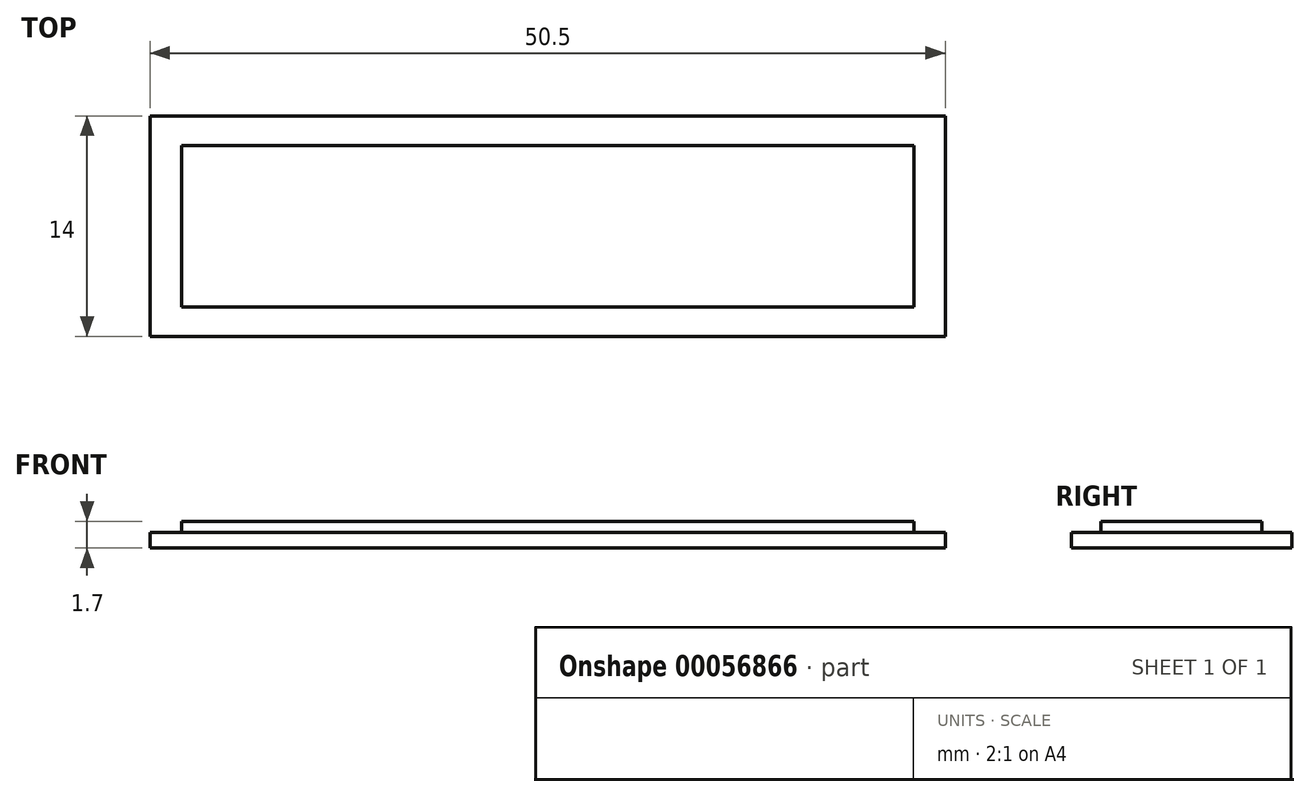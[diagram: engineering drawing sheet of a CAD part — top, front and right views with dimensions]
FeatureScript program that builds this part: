
annotation { "Feature Type Name" : "Feature", "Feature Type Description" : "" }
export const myFeature = defineFeature(function(context is Context, id is Id, definition is map)
    precondition{}
    {
        {
            var Q0;
            Q0=qCreatedBy(makeId("Top.planeOp"),FACE);
            var sketch = newSketch(context, id + "F0", { "sketchPlane" : qUnion([Q0])});
            skLineSegment(sketch, "E0", {"start": v(0, 7) * mm, "end": v(0, -7) * mm, "construction": true});
            skLineSegment(sketch, "E1.0", {"start": v(-23.25, 7) * mm, "end": v(-23.25, -7) * mm, "construction": true});
            skLineSegment(sketch, "E2.0", {"start": v(23.25, 7) * mm, "end": v(23.25, -7) * mm, "construction": true});
            skLineSegment(sketch, "E3", {"start": v(-27.72, 0) * mm, "end": v(23.25, 0) * mm, "construction": true});
            skLineSegment(sketch, "E4.0", {"start": v(-25.25, -7) * mm, "end": v(27.82, -7) * mm, "construction": true});
            skLineSegment(sketch, "E5.0", {"start": v(-25.25, 7) * mm, "end": v(27.82, 7) * mm, "construction": true});
            skLineSegment(sketch, "E6.0", {"start": v(-25.25, -5.12) * mm, "end": v(23.25, -5.12) * mm, "construction": true});
            skLineSegment(sketch, "E7.0", {"start": v(-25.25, 5.12) * mm, "end": v(23.25, 5.12) * mm, "construction": true});
            skLineSegment(sketch, "E8.0", {"start": v(25.25, 7) * mm, "end": v(25.25, -7) * mm, "construction": true});
            skLineSegment(sketch, "E9.0", {"start": v(-25.25, 7) * mm, "end": v(-25.25, -7) * mm, "construction": true});
            skPoint(sketch, "E10.orphan", {"position": v(0, 12.03) * mm});
            skLineSegment(sketch, "E11", {"start": v(-25.25, 7) * mm, "end": v(25.25, 7) * mm});
            skLineSegment(sketch, "E12", {"start": v(25.25, -7) * mm, "end": v(-25.25, -7) * mm});
            skLineSegment(sketch, "E13", {"start": v(-25.25, -7) * mm, "end": v(-25.25, 7) * mm});
            skLineSegment(sketch, "E14", {"start": v(25.25, 7) * mm, "end": v(25.25, -7) * mm});
            skLineSegment(sketch, "E15", {"start": v(23.25, -5.12) * mm, "end": v(23.25, 5.12) * mm});
            skLineSegment(sketch, "E16", {"start": v(23.25, 5.13) * mm, "end": v(-23.25, 5.12) * mm});
            skLineSegment(sketch, "E17", {"start": v(-23.25, 5.12) * mm, "end": v(-23.25, -5.12) * mm});
            skLineSegment(sketch, "E18", {"start": v(-23.25, -5.12) * mm, "end": v(23.25, -5.12) * mm});
            skLineSegment(sketch, "E19.trimOffspring", {"start": v(25.25, -5.12) * mm, "end": v(27.82, -5.12) * mm, "construction": true});
            skLineSegment(sketch, "E20.trimOffspring", {"start": v(25.25, 0) * mm, "end": v(27.82, 0) * mm, "construction": true});
            skLineSegment(sketch, "E21.trimOffspring", {"start": v(25.25, 5.12) * mm, "end": v(27.82, 5.12) * mm, "construction": true});
            skSolve(sketch);
        }
        {
            var Q0;
            Q0=makeQuery(id+"F0.imprint","IMPRINT",FACE,{"disambiguationData":[TD([[makeQuery(id+"F0.imprint","IMPRINT",EDGE,{"derivedFrom":sQuery(id+"F0.wireOp",EDGE,"E15")}),1.0]])]});
            extrude(context, id + "F1", {"entities" : qUnion([Q0]), "depth" : 1.7 * mm});
        }
        {
            var Q0;
            Q0=makeQuery(id+"F0.imprint","IMPRINT",FACE,{"disambiguationData":[TD([[makeQuery(id+"F0.imprint","IMPRINT",EDGE,{"derivedFrom":sQuery(id+"F0.wireOp",EDGE,"E11")}),-1.0]])]});
            extrude(context, id + "F2", {"entities" : qUnion([Q0]), "operationType" : NewBodyOperationType.ADD, "depth" : 1 * mm});
        }
    });
